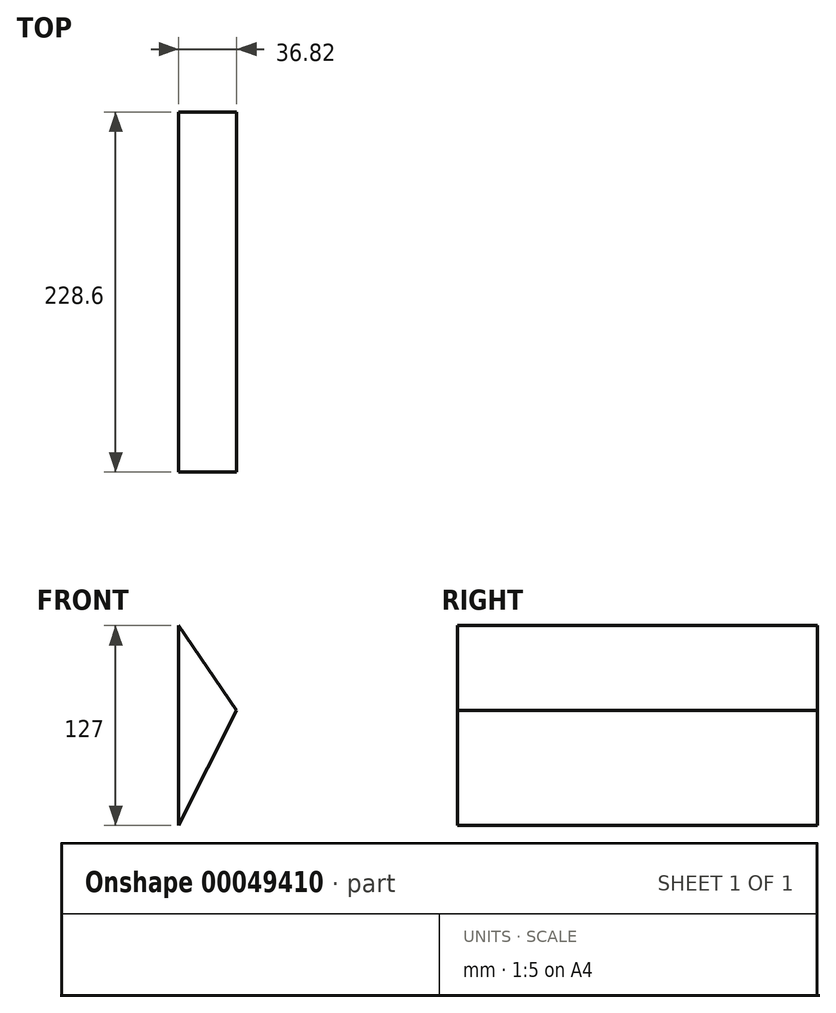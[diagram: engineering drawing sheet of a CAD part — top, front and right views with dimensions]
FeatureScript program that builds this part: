
annotation { "Feature Type Name" : "Feature", "Feature Type Description" : "" }
export const myFeature = defineFeature(function(context is Context, id is Id, definition is map)
    precondition{}
    {
        {
            var Q0;
            Q0=qCreatedBy(makeId("Front.planeOp"),FACE);
            var sketch = newSketch(context, id + "F0", { "sketchPlane" : qUnion([Q0])});
            skLineSegment(sketch, "E0.bottom", {"start": v(-86.19, 78.44) * mm, "end": v(117.01, 78.44) * mm});
            skLineSegment(sketch, "E0.top", {"start": v(-86.19, -48.56) * mm, "end": v(117.01, -48.56) * mm});
            skLineSegment(sketch, "E0.left", {"start": v(-86.19, 78.44) * mm, "end": v(-86.19, -48.56) * mm});
            skLineSegment(sketch, "E0.right", {"start": v(117.01, 78.44) * mm, "end": v(117.01, -48.56) * mm});
            skLineSegment(sketch, "E1", {"start": v(117.01, 78.44) * mm, "end": v(153.83, 24.5) * mm});
            skLineSegment(sketch, "E2", {"start": v(153.83, 24.5) * mm, "end": v(117.01, -48.56) * mm});
            skSolve(sketch);
        }
        {
            var Q0;
            Q0=makeQuery(id+"F0.imprint","IMPRINT",FACE,{"disambiguationData":[TD([[makeQuery(id+"F0.imprint","IMPRINT",EDGE,{"derivedFrom":sQuery(id+"F0.wireOp",EDGE,"E0.right")}),1.0]])]});
            extrude(context, id + "F1", {"entities" : qUnion([Q0]), "oppositeDirection" : true, "depth" : 25.4 * mm});
        }
        {
            var Q0;
            Q0=makeQuery(id+"F1.opExtrude","CAP_FACE",FACE,{"disambiguationData":[OSD([sQuery(id+"F0.wireOp",EDGE,"E0.right"),sQuery(id+"F0.wireOp",EDGE,"E1"),sQuery(id+"F0.wireOp",EDGE,"E2")])],"isStart":true});
            extrude(context, id + "F2", {"entities" : qUnion([Q0]), "operationType" : NewBodyOperationType.ADD, "depth" : 203.2 * mm});
        }
    });
